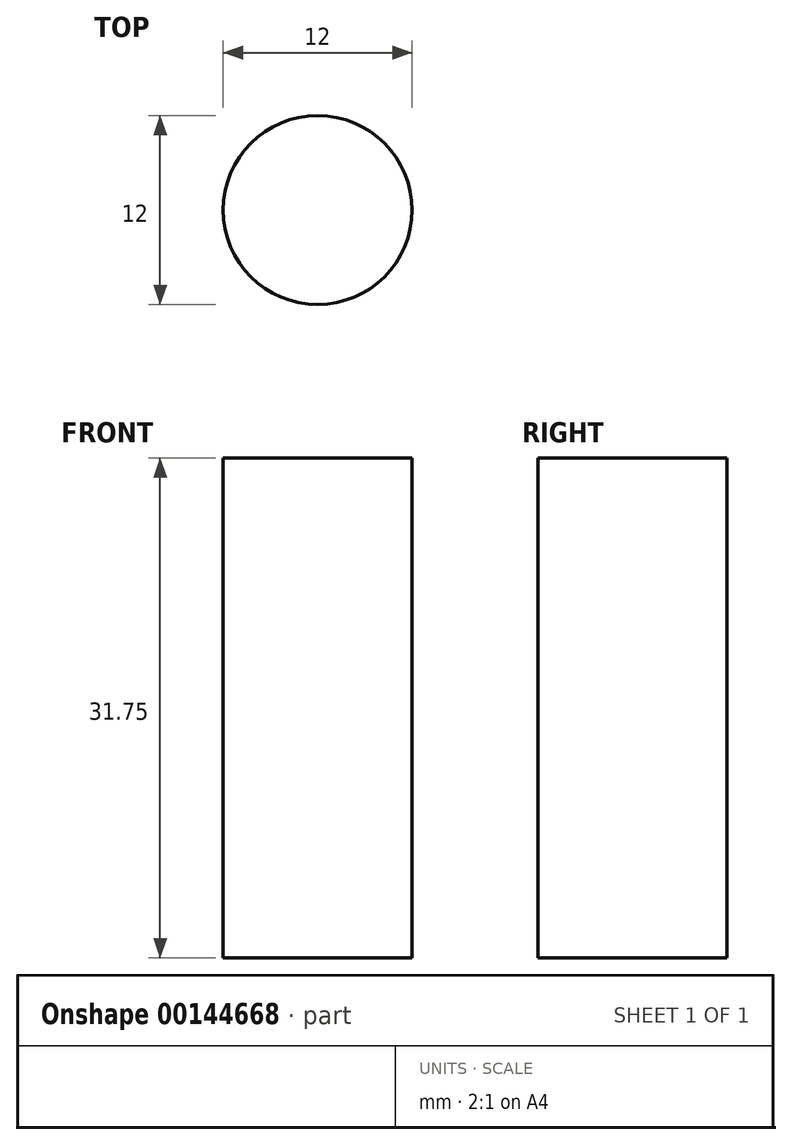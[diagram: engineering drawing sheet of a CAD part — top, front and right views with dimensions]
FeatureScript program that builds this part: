
annotation { "Feature Type Name" : "Feature", "Feature Type Description" : "" }
export const myFeature = defineFeature(function(context is Context, id is Id, definition is map)
    precondition{}
    {
        {
            var Q0;
            Q0=qCreatedBy(makeId("Top.planeOp"),FACE);
            var sketch = newSketch(context, id + "F0", { "sketchPlane" : qUnion([Q0])});
            skCircle(sketch, "E0", {"center": v(0, 0) * mm, "radius": 6 * mm});
            skSolve(sketch);
        }
        {
            var Q0;
            Q0=makeQuery(id+"F0.imprint","IMPRINT",FACE,{"disambiguationData":[TD([[makeQuery(id+"F0.imprint","IMPRINT",EDGE,{"derivedFrom":sQuery(id+"F0.wireOp",EDGE,"E0")}),1.0]])]});
            extrude(context, id + "F1", {"entities" : qUnion([Q0]), "depth" : 31.75 * mm});
        }
    });
